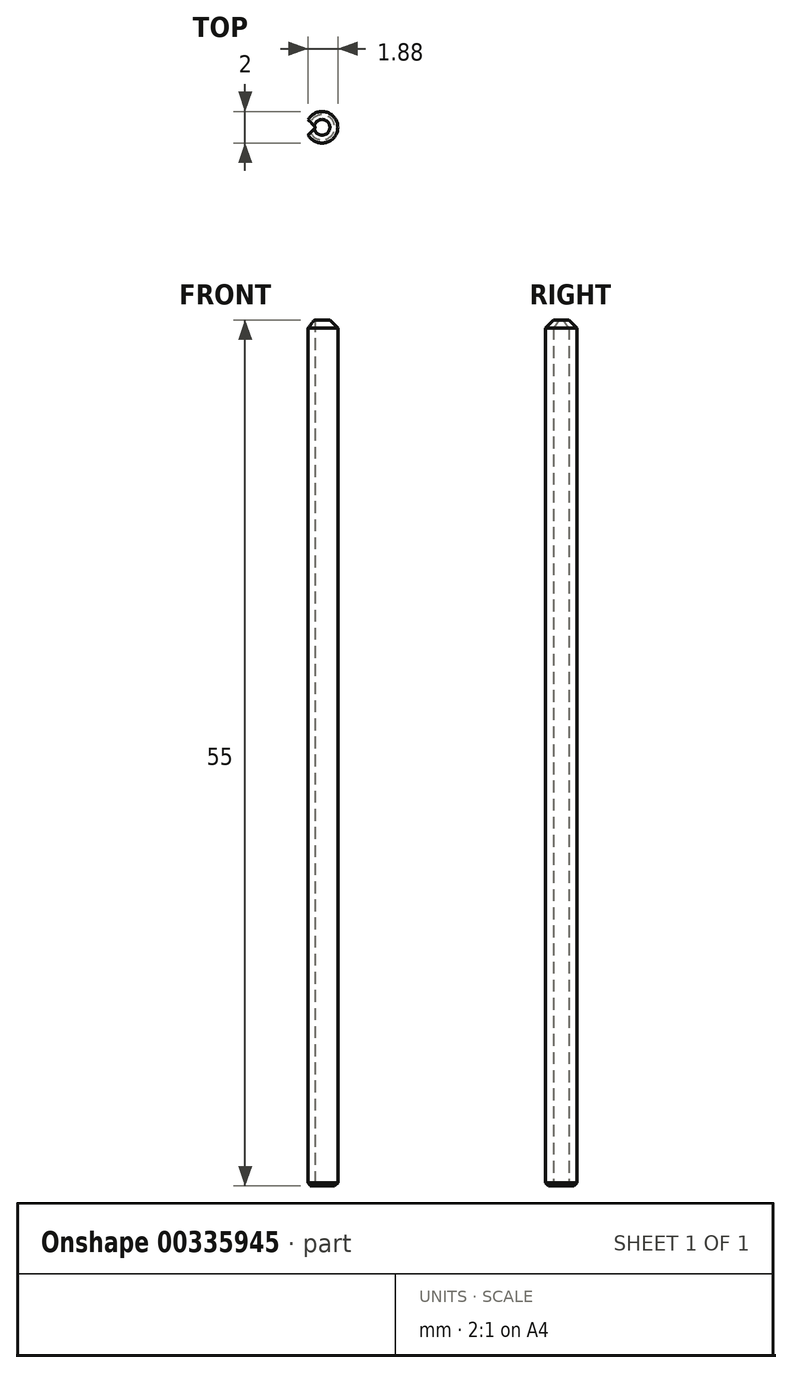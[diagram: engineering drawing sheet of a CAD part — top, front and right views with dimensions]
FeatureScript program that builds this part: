
annotation { "Feature Type Name" : "Feature", "Feature Type Description" : "" }
export const myFeature = defineFeature(function(context is Context, id is Id, definition is map)
    precondition{}
    {
        {
            var Q0;
            Q0=qCreatedBy(makeId("Top.planeOp"),FACE);
            var sketch = newSketch(context, id + "F0", { "sketchPlane" : qUnion([Q0])});
            skCircle(sketch, "E0", {"center": v(0, 0) * mm, "radius": 1 * mm});
            skCircle(sketch, "E1", {"center": v(-1.1, 0) * mm, "radius": 0.5 * mm, "construction": true});
            skPoint(sketch, "E2", {"position": v(-1.6, 0) * mm});
            skPoint(sketch, "E3", {"position": v(1, 0) * mm});
            skLineSegment(sketch, "E4", {"start": v(-0.47, 0.07) * mm, "end": v(-0.88, 0.48) * mm});
            skLineSegment(sketch, "E5", {"start": v(-0.47, -0.07) * mm, "end": v(-0.88, -0.48) * mm});
            skPoint(sketch, "E6.visualSharp", {"position": v(-0.4, 0) * mm});
            skArc(sketch, "E6.filletArc", {"start": v(-0.47, -0.07) * mm, "mid": v(-0.44, 0) * mm, "end": v(-0.47, 0.07) * mm});
            skSolve(sketch);
        }
        {
            var Q0;
            {var subQ0=sQuery(id+"F0.wireOp",EDGE,"E4");Q0=makeQuery(id+"F0.imprint","IMPRINT",FACE,{"disambiguationData":[TD([[makeQuery(id+"F0.imprint","IMPRINT",EDGE,{"derivedFrom":subQ0}),-1.0]])]});}
            extrude(context, id + "F1", {"entities" : qUnion([Q0]), "endBound" : BoundingType.SYMMETRIC, "depth" : 55 * mm});
        }
        {
            var Q0;
            Q0=makeQuery(id+"F1.opExtrude","CAP_EDGE",EDGE,{"disambiguationData":[OSD([sQuery(id+"F0.wireOp",EDGE,"E0")])],"isStart":false});
            chamfer(context, id + "F2", {"entities" : qUnion([Q0]), "width" : 0.5 * mm, "tangentPropagation" : true});
        }
        {
            var Q0;
            Q0=makeQuery(id+"F1.opExtrude","CAP_EDGE",EDGE,{"disambiguationData":[OSD([sQuery(id+"F0.wireOp",EDGE,"E0")])],"isStart":true});
            chamfer(context, id + "F3", {"entities" : qUnion([Q0]), "width" : 0.2 * mm, "tangentPropagation" : true});
        }
    });
